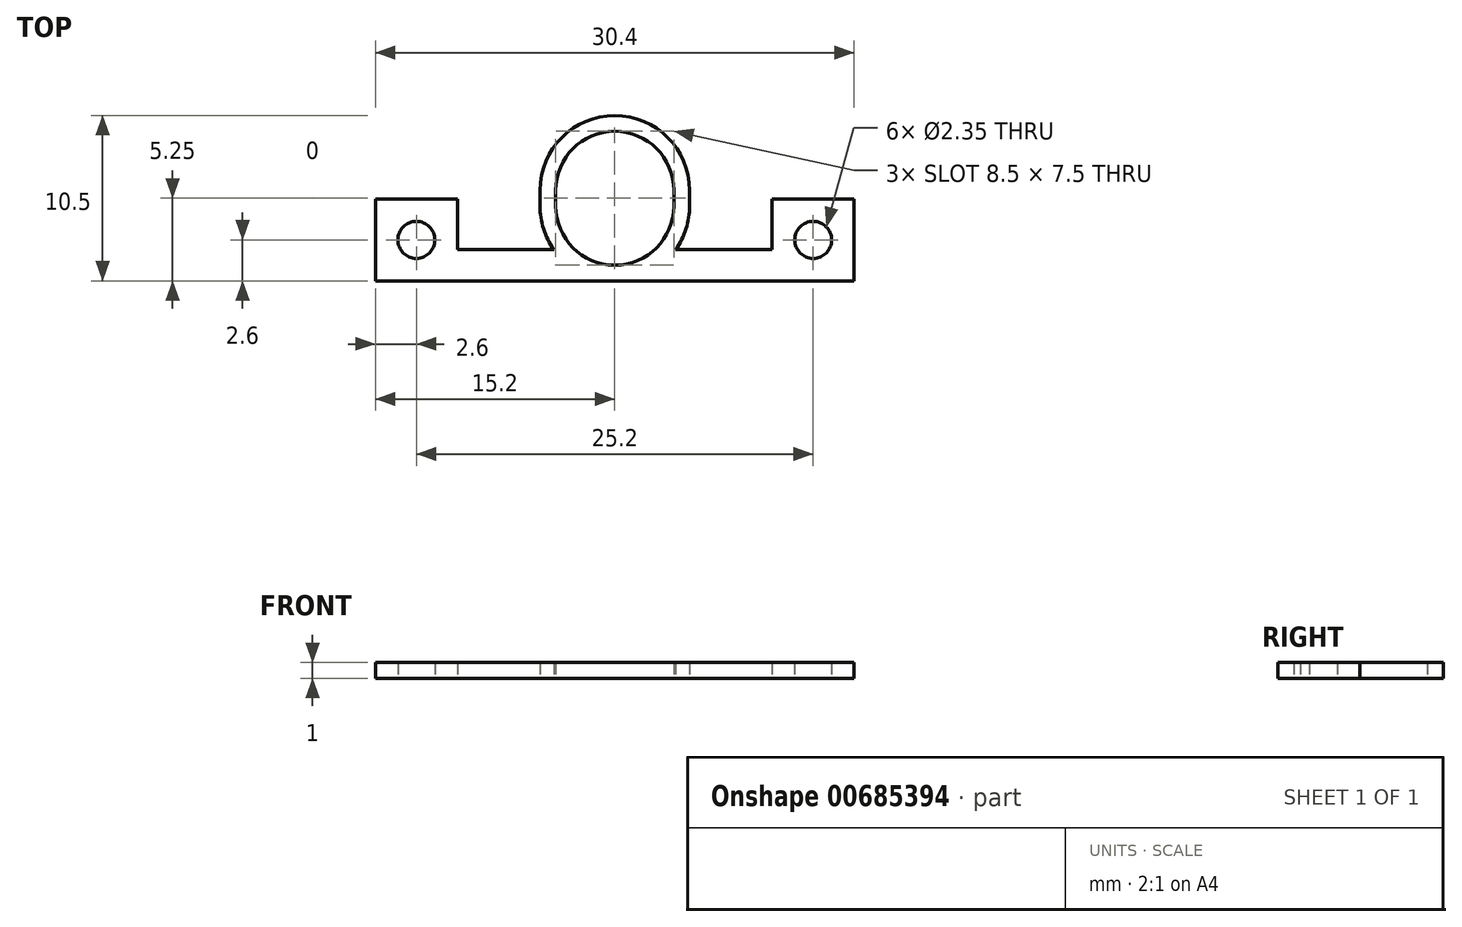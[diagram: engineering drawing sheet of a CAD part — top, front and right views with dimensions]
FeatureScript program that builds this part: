
annotation { "Feature Type Name" : "Feature", "Feature Type Description" : "" }
export const myFeature = defineFeature(function(context is Context, id is Id, definition is map)
    precondition{}
    {
        {
            var Q0;
            Q0=qCreatedBy(makeId("Top.planeOp"),FACE);
            var sketch = newSketch(context, id + "F0", { "sketchPlane" : qUnion([Q0])});
            skArc(sketch, "E0", {"start": v(4.75, 0) * mm, "mid": v(0, 4.75) * mm, "end": v(-4.75, 0) * mm});
            skLineSegment(sketch, "E1.left", {"start": v(-3.75, 0) * mm, "end": v(-3.75, -1) * mm});
            skLineSegment(sketch, "E1.right", {"start": v(3.75, 0) * mm, "end": v(3.75, -1) * mm});
            skArc(sketch, "E2", {"start": v(-3.75, -1) * mm, "mid": v(0, -4.75) * mm, "end": v(3.75, -1) * mm});
            skArc(sketch, "E3", {"start": v(-4.75, -1) * mm, "mid": v(-4.53, -2.44) * mm, "end": v(-3.87, -3.75) * mm});
            skArc(sketch, "E4.trimOffspring", {"start": v(3.75, 0) * mm, "mid": v(0, 3.75) * mm, "end": v(-3.75, 0) * mm});
            skLineSegment(sketch, "E5", {"start": v(-4.75, 0) * mm, "end": v(-4.75, -1) * mm});
            skLineSegment(sketch, "E6", {"start": v(4.75, 0) * mm, "end": v(4.75, -1) * mm});
            skPoint(sketch, "E7.oppositeSnap0", {"position": v(0, -5.75) * mm});
            skLineSegment(sketch, "E7.bottom", {"start": v(3.87, -3.75) * mm, "end": v(10, -3.75) * mm});
            skLineSegment(sketch, "E7.top", {"start": v(0, -5.75) * mm, "end": v(10, -5.75) * mm});
            skLineSegment(sketch, "E8.bottom", {"start": v(-3.87, -3.75) * mm, "end": v(-10, -3.75) * mm});
            skLineSegment(sketch, "E8.top", {"start": v(0, -5.75) * mm, "end": v(-10, -5.75) * mm});
            skLineSegment(sketch, "E9.bottom", {"start": v(10, -5.75) * mm, "end": v(15.2, -5.75) * mm});
            skLineSegment(sketch, "E9.top", {"start": v(10, -0.55) * mm, "end": v(15.2, -0.55) * mm});
            skLineSegment(sketch, "E9.left", {"start": v(10, -3.75) * mm, "end": v(10, -0.55) * mm});
            skLineSegment(sketch, "E9.right", {"start": v(15.2, -5.75) * mm, "end": v(15.2, -0.55) * mm});
            skLineSegment(sketch, "E10.bottom", {"start": v(-10, -5.75) * mm, "end": v(-15.2, -5.75) * mm});
            skLineSegment(sketch, "E10.top", {"start": v(-10, -0.55) * mm, "end": v(-15.2, -0.55) * mm});
            skLineSegment(sketch, "E10.left", {"start": v(-10, -3.75) * mm, "end": v(-10, -0.55) * mm});
            skLineSegment(sketch, "E10.right", {"start": v(-15.2, -5.75) * mm, "end": v(-15.2, -0.55) * mm});
            skCircle(sketch, "E11", {"center": v(-12.6, -3.15) * mm, "radius": 1.18 * mm});
            skPoint(sketch, "E11.centerSnap0", {"position": v(-10, -3.15) * mm});
            skPoint(sketch, "E11.centerSnap1", {"position": v(-12.6, -0.55) * mm});
            skCircle(sketch, "E12", {"center": v(12.6, -3.15) * mm, "radius": 1.18 * mm});
            skPoint(sketch, "E12.centerSnap0", {"position": v(12.6, -0.55) * mm});
            skPoint(sketch, "E12.centerSnap1", {"position": v(10, -3.15) * mm});
            skArc(sketch, "E13.trimOffspring", {"start": v(3.87, -3.75) * mm, "mid": v(4.53, -2.44) * mm, "end": v(4.75, -1) * mm});
            skSolve(sketch);
        }
        {
            var Q0;
            Q0=makeQuery(id+"F0.imprint","IMPRINT",FACE,{"disambiguationData":[TD([[makeQuery(id+"F0.imprint","IMPRINT",EDGE,{"derivedFrom":sQuery(id+"F0.wireOp",EDGE,"E0")}),1.0]])]});
            extrude(context, id + "F1", {"entities" : qUnion([Q0]), "depth" : 1 * mm, "offsetDistance" : 25 * mm});
        }
    });
